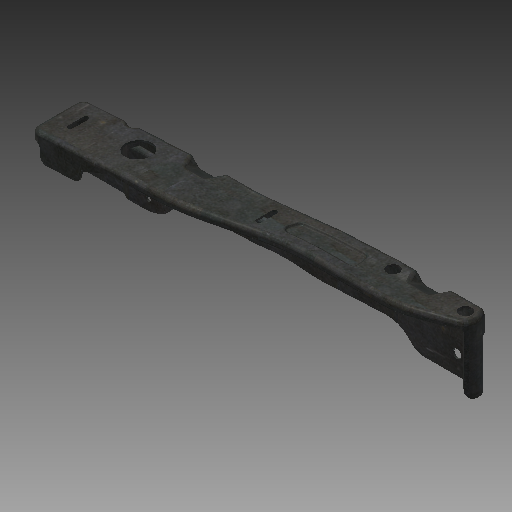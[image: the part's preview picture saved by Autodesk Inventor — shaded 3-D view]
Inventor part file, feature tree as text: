
AUTODESK INVENTOR PART (.ipt)
format: ipt  version: 2019 (Build 230136000, 136)  size: 1,337,856 bytes
history: native  units: mm
features: fillet x21, sketch x21, extrude x18, hole x4, plane x3, chamfer x3, projected_geometry x3, shell x1, other x1
ambient origin geometry x8: Origin, YZ Plane, XZ Plane, XY Plane, X Axis, Y Axis, Z Axis, Center Point
bodies: Solid1 (feature_tree)
feature tree (75):
  extrude  "Extrusion1"  Depth=85.0mm
  extrude  "Extrusion2"  Depth=65.0mm
  fillet  "Fillet1"  Radius=0.698132mm
  extrude  "Extrusion3"  Depth=11.34464mm
  extrude  "Extrusion4"  Depth=17.0mm
  fillet  "Fillet4"  Radius=30.0mm
  fillet  "Fillet5"  Radius=63.0mm
  fillet  "Fillet6"  Radius=165.0mm
  fillet  "Fillet7"  Radius=112.0mm
  plane  "Work Plane1"
  extrude  "Extrusion9"  Depth=125.0mm
  chamfer  "Chamfer2"  Distance=80.0mm
  chamfer  "Chamfer3"  Distance=80.0mm
  fillet  "Fillet13"  Radius=500.0mm
  fillet  "Fillet14"  Radius=100.0mm
  plane  "Work Plane2"
  extrude  "Extrusion10"  Depth=60.0mm
  chamfer  "Chamfer4"  Distance=80.0mm
  fillet  "Fillet15"  Radius=4.0mm
  fillet  "Fillet16"  Radius=55.0mm
  fillet  "Fillet8"  Radius=10.0mm
  shell  "Shell1"  Thickness=10.0mm
  extrude  "Extrusion5"  Depth=3.0mm
  extrude  "Extrusion6"  Depth=2.2mm
  extrude  "Extrusion7"  Depth=66.0mm
  extrude  "Extrusion8"  Depth=4.5mm
  fillet  "Fillet9"  Radius=36.8mm
  fillet  "Fillet10"  Radius=54.0mm
  fillet  "Fillet11"  Radius=62.0mm
  fillet  "Fillet12"  Radius=7.0mm
  extrude  "Extrusion11"  Depth=50.0mm
  fillet  "Fillet17"  Radius=35.0mm
  fillet  "Fillet18"  Radius=8.0mm
  extrude  "Extrusion12"  Depth=10.0mm
  extrude  "Extrusion13"  Depth=20.0mm
  fillet  "Fillet19"  Radius=15.358897mm
  fillet  "Fillet20"  Radius=48.0mm
  extrude  "Extrusion14"  Depth=10.0mm
  extrude  "Extrusion15"  Depth=10.0mm
  fillet  "Fillet21"  Radius=435.0mm
  fillet  "Fillet22"  Radius=6.0mm
  fillet  "Fillet23"  Radius=8.0mm
  plane  "Work Plane3"
  hole  "Hole1"  [1 undecoded]
  hole  "Hole2"  [1 undecoded]
  hole  "Hole3"  [1 undecoded]
  hole  "Hole4"  [1 undecoded]
  extrude  "Extrusion17"  Depth=6.0mm
  extrude  "Extrusion18"  Depth=2.2mm TaperAngle=0.0deg
  sketch  "Sketch23"  dims[d56=6.0mm d57=0.0mm d58=10.0mm]
  extrude  "Extrusion19"  Depth=5.0mm
  sketch  "Sketch25"  dims[d63=16.0mm d64=6.5mm d65=31.0mm d66=435.0mm d67=6.0mm d68=8.0mm d69=4.0mm d72=45.0mm d73=0.0mm d75=73.0mm d76=0.0mm d77=6.0mm d78=6.0mm d79=2.2mm d80=0.0mm d81=5.0mm d82=6.0mm d83=2.5mm d84=0.3mm d85=10.0mm d86=5.0mm d87=-150.0mm d89=12.0mm d90=60.0deg d91=15.0mm d92=40.0mm d93=0.0mm d97=8.0mm d98=20.483362mm d99=60.0deg d100=8.0mm d101=20.483362mm d102=60.0deg d103=5.0mm d104=5.0mm d106=12.0mm d107=60.0deg d108=15.0mm d109=40.0mm d110=0.0mm d111=8.0mm d112=20.483362mm d113=60.0deg d114=5.0mm d115=5.0mm d116=18.0mm d117=38.0mm d118=21.0mm d119=3.839724mm d120=8.0mm d121=11.519173mm d122=120.0mm d123=0.349066mm d124=45.0mm d125=2.094395mm d126=85.0mm d127=8.726646mm d128=10.0mm d129=50.0mm d130=28.0mm d131=12.0mm d132=150.0mm d133=40.0mm d134=40.0mm d135=0.0mm d136=20.0mm d137=10.0mm d138=9.5mm d139=9.5mm d140=9.5mm d142=40.0mm d144=19.754598mm d145=72.697526mm d147=10.925504mm d148=5.0mm d149=16.982548mm d150=2.2mm d151=0.0mm d152=2.2mm d153=2.2mm d154=0.0mm d155=2.2mm d156=2.2mm d157=10.5mm d158=65.302mm d159=27.606mm d160=10.0mm d161=0.0mm d162=10.5mm d163=84.452432mm d164=41.142708mm d165=10.0mm d166=0.0mm d167=2.0mm d168=2.0mm d169=2.0mm d178=90.0deg d179=14.65mm d180=6.0mm d181=4.0mm d182=2.0mm d183=90.0deg d184=8.0mm d185=20.594885mm d186=365.527745mm d187=1.647225mm d192=-250.0mm d193=42.041985mm d202=10.0mm d203=15.0mm d204=5.9mm d205=6.0mm d206=4.0mm d207=2.0mm d208=90.0deg d209=8.0mm d210=20.594885mm d211=15.0mm d212=120.0mm d213=5.9mm d214=6.0mm d215=4.0mm d216=2.0mm d217=90.0deg d218=8.0mm d219=20.594885mm d220=120.0mm d221=40.0mm d222=5.9mm d223=6.0mm d224=4.0mm d225=2.0mm d226=90.0deg d227=8.0mm d228=20.594885mm d229=0.0mm d230=0.0mm d231=0.0mm d232=30.0mm d233=10.0mm d234=0.0mm d235=6.0mm d236=18.0mm d237=25.0mm d238=25.0mm d239=10.0mm d240=0.0mm d241=18.0mm d242=6.0mm d243=10.0mm d244=0.0mm]
  sketch  "Sketch2"  dims[d0=210.0mm d1=85.0mm]
  sketch  "Sketch3"  dims[d2=1.22173mm d3=65.0mm d4=0.698132mm]
  sketch  "Sketch4"  dims[d5=460.0mm d6=11.34464mm]
  sketch  "Sketch5"  dims[d7=120.0deg d8=17.0mm d9=30.0mm d10=63.0mm d11=165.0mm d12=112.0mm]
  sketch  "Sketch6"  dims[d13=2.356194mm d14=125.0mm]
  sketch  "Sketch7"  dims[d15=10.0mm]
  sketch  "Sketch8"  dims[d16=15.0mm]
  sketch  "Sketch9"  dims[d17=40.0mm]
  sketch  "Sketch10"  dims[d18=120.0mm]
  sketch  "Sketch11"  dims[d19=250.0mm d20=80.0mm d21=0.0mm]
  sketch  "Sketch12"  dims[d22=0.610865mm d23=80.0mm d24=0.0mm d25=500.0mm d26=100.0mm]
  sketch  "Sketch13"  dims[d27=4.5mm d28=60.0mm]
  sketch  "Sketch14"  dims[d29=17.0mm d30=80.0mm d31=0.0mm d32=4.0mm d33=55.0mm d34=0.0mm d38=10.0mm d39=10.0mm]
  sketch  "Sketch15"  dims[d40=3.0mm d41=3.0mm]
  sketch  "Sketch16"  dims[d42=5.0mm d43=2.2mm]
  other  "Work Axis1"
  sketch  "Sketch17"  dims[d44=62.0mm d45=66.0mm]
  sketch  "Sketch21"  dims[d46=27.0mm d47=4.5mm d48=36.8mm d49=54.0mm d50=62.0mm d51=7.0mm]
  sketch  "Sketch22"  dims[d52=44.0mm d53=50.0mm d54=35.0mm d55=8.0mm]
  projected_geometry  "Projected Loop1"
  sketch  "Sketch24"  dims[d59=6.5mm d60=20.0mm d61=15.358897mm d62=48.0mm]
  projected_geometry  "Project Cut Edges1"
  projected_geometry  "Project Cut Edges2"
note: 4 required parameter values undecoded (feature->parameter linkage not recoverable at this tier; creation-order binding heuristic only, values carry confidence <= 0.55)
